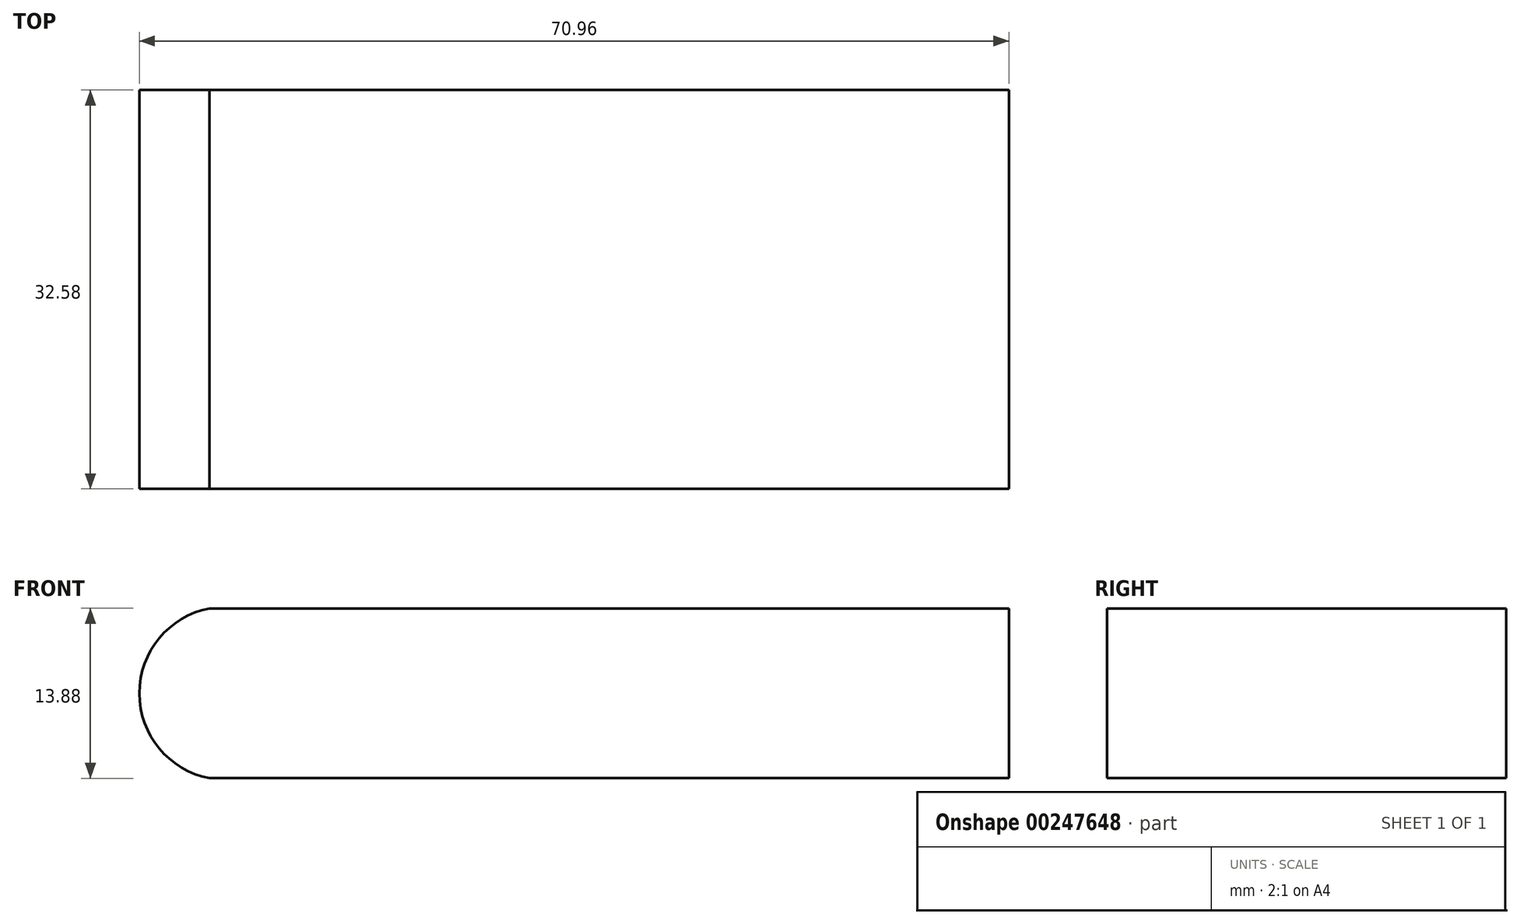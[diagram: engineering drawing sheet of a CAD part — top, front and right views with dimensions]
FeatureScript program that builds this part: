
annotation { "Feature Type Name" : "Feature", "Feature Type Description" : "" }
export const myFeature = defineFeature(function(context is Context, id is Id, definition is map)
    precondition{}
    {
        {
            var Q0;
            Q0=qCreatedBy(makeId("Front.planeOp"),FACE);
            var sketch = newSketch(context, id + "F0", { "sketchPlane" : qUnion([Q0])});
            skLineSegment(sketch, "E0.bottom", {"start": v(35.48, -6.94) * mm, "end": v(-35.48, -6.94) * mm});
            skLineSegment(sketch, "E0.top", {"start": v(35.47, 6.93) * mm, "end": v(-35.48, 6.93) * mm});
            skLineSegment(sketch, "E0.left", {"start": v(35.48, -6.94) * mm, "end": v(35.48, 6.93) * mm});
            skLineSegment(sketch, "E0.right", {"start": v(-35.47, -6.94) * mm, "end": v(-35.48, 6.93) * mm});
            skPoint(sketch, "E0.middle", {"position": v(0, 0) * mm});
            skLineSegment(sketch, "E1", {"start": v(-29.76, 6.93) * mm, "end": v(-29.76, -6.94) * mm, "construction": true});
            skPoint(sketch, "E2", {"position": v(-35.48, 0) * mm});
            skArc(sketch, "E3", {"start": v(-29.76, 6.93) * mm, "mid": v(-35.48, 0) * mm, "end": v(-29.76, -6.94) * mm});
            skSolve(sketch);
        }
        {
            var Q0;
            {var subQ4=sQuery(id+"F0.wireOp",EDGE,"E0.left");Q0=makeQuery(id+"F0.imprint","IMPRINT",FACE,{"disambiguationData":[TD([[makeQuery(id+"F0.imprint","IMPRINT",EDGE,{"derivedFrom":subQ4}),1.0]])]});}
            extrude(context, id + "F1", {"entities" : qUnion([Q0]), "depth" : 32.58 * mm, "symmetric" : true});
        }
    });
